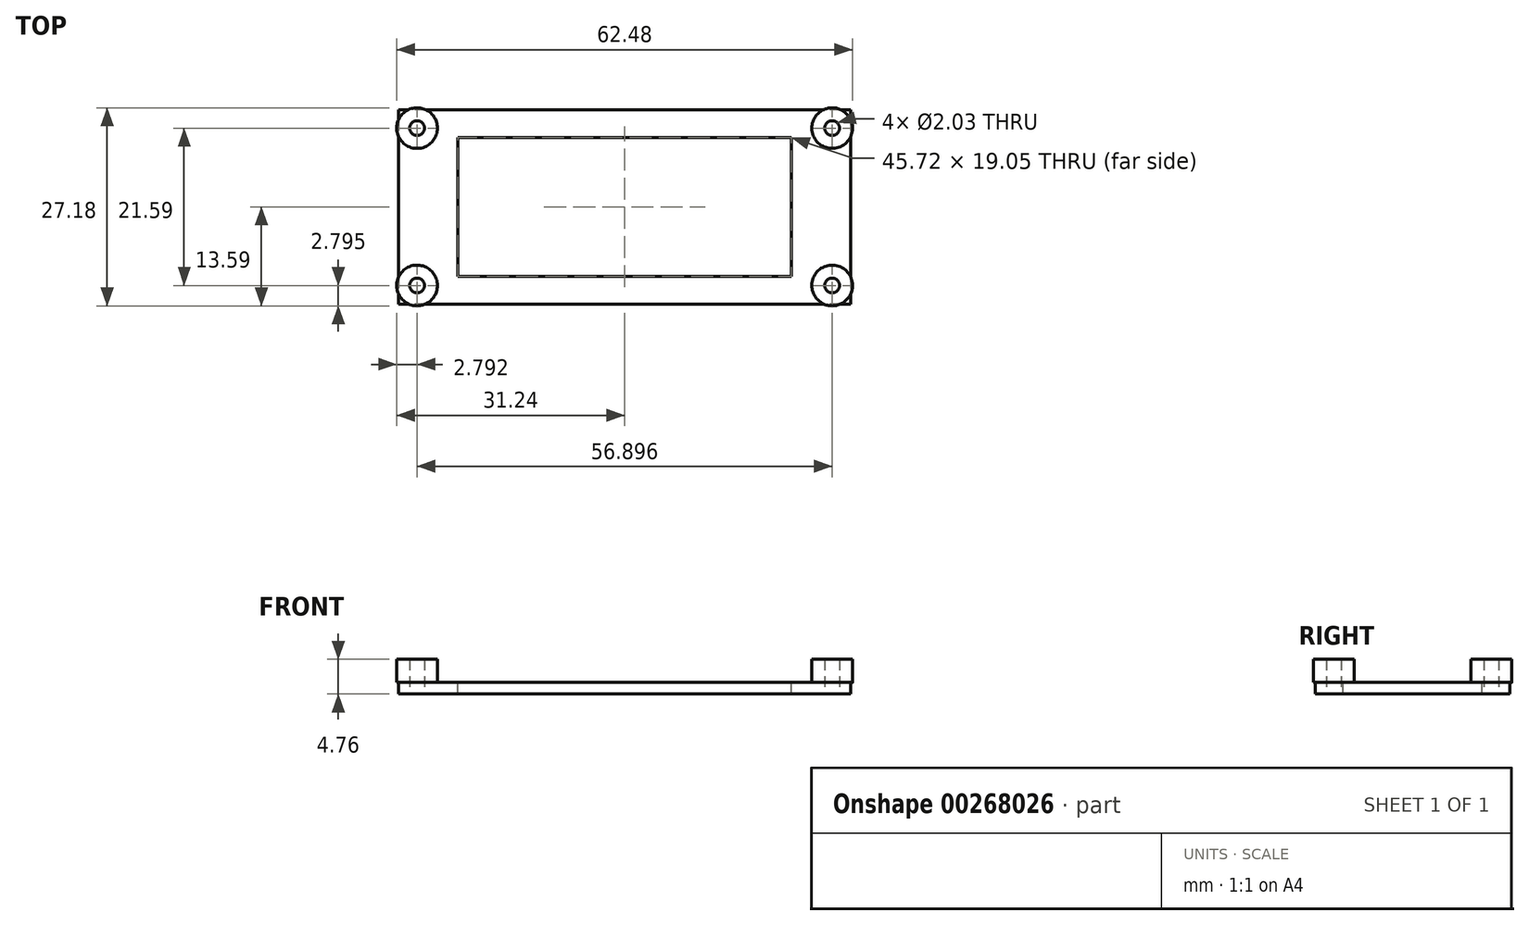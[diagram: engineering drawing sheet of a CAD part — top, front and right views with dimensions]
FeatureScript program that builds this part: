
annotation { "Feature Type Name" : "Feature", "Feature Type Description" : "" }
export const myFeature = defineFeature(function(context is Context, id is Id, definition is map)
    precondition{}
    {
        {
            var Q0;
            Q0=qCreatedBy(makeId("Top.planeOp"),FACE);
            var sketch = newSketch(context, id + "F0", { "sketchPlane" : qUnion([Q0])});
            skLineSegment(sketch, "E0.bottom", {"start": v(30.99, 13.33) * mm, "end": v(-30.99, 13.34) * mm});
            skLineSegment(sketch, "E0.top", {"start": v(30.99, -13.34) * mm, "end": v(-30.99, -13.34) * mm});
            skLineSegment(sketch, "E0.left", {"start": v(30.99, 13.33) * mm, "end": v(30.99, -13.34) * mm});
            skLineSegment(sketch, "E0.right", {"start": v(-30.99, 13.34) * mm, "end": v(-30.99, -13.34) * mm});
            skPoint(sketch, "E0.middle", {"position": v(0, 0) * mm});
            skSolve(sketch);
        }
        {
            var Q0;
            Q0=makeQuery(id+"F0.imprint","IMPRINT",FACE,{"disambiguationData":[TD([[makeQuery(id+"F0.imprint","IMPRINT",EDGE,{"derivedFrom":sQuery(id+"F0.wireOp",EDGE,"E0.bottom")}),1.0]])]});
            extrude(context, id + "F1", {"entities" : qUnion([Q0]), "depth" : 1.59 * mm});
        }
        {
            var Q0;
            Q0=makeQuery(id+"F1.opExtrude","CAP_FACE",FACE,{"disambiguationData":[OSD([sQuery(id+"F0.wireOp",EDGE,"E0.bottom"),sQuery(id+"F0.wireOp",EDGE,"E0.top"),sQuery(id+"F0.wireOp",EDGE,"E0.left"),sQuery(id+"F0.wireOp",EDGE,"E0.right")])],"isStart":false});
            var sketch = newSketch(context, id + "F2", { "sketchPlane" : qUnion([Q0])});
            skLineSegment(sketch, "E1.bottom", {"start": v(28.45, -13.34) * mm, "end": v(30.99, -13.34) * mm, "construction": true});
            skLineSegment(sketch, "E1.top", {"start": v(28.45, -10.8) * mm, "end": v(30.99, -10.8) * mm, "construction": true});
            skLineSegment(sketch, "E1.left", {"start": v(28.45, -13.34) * mm, "end": v(28.45, -10.8) * mm, "construction": true});
            skLineSegment(sketch, "E1.right", {"start": v(30.99, -13.34) * mm, "end": v(30.99, -10.8) * mm, "construction": true});
            skCircle(sketch, "E2", {"center": v(28.45, -10.8) * mm, "radius": 1.02 * mm});
            skCircle(sketch, "E3", {"center": v(28.45, -10.8) * mm, "radius": 2.8 * mm});
            skCircle(sketch, "E4", {"center": v(-28.45, 10.8) * mm, "radius": 1.02 * mm});
            skCircle(sketch, "E5", {"center": v(-28.45, 10.8) * mm, "radius": 2.8 * mm});
            skCircle(sketch, "E6", {"center": v(-28.45, -10.8) * mm, "radius": 1.02 * mm});
            skCircle(sketch, "E7", {"center": v(-28.45, -10.8) * mm, "radius": 2.8 * mm});
            skLineSegment(sketch, "E8.bottom", {"start": v(30.99, 13.33) * mm, "end": v(28.45, 13.33) * mm, "construction": true});
            skLineSegment(sketch, "E8.top", {"start": v(30.99, 10.8) * mm, "end": v(28.45, 10.8) * mm, "construction": true});
            skLineSegment(sketch, "E8.left", {"start": v(30.99, 13.33) * mm, "end": v(30.99, 10.8) * mm, "construction": true});
            skLineSegment(sketch, "E8.right", {"start": v(28.45, 13.33) * mm, "end": v(28.45, 10.8) * mm, "construction": true});
            skLineSegment(sketch, "E9.bottom", {"start": v(-30.99, 13.34) * mm, "end": v(-28.45, 13.34) * mm, "construction": true});
            skLineSegment(sketch, "E9.top", {"start": v(-30.99, 10.8) * mm, "end": v(-28.45, 10.8) * mm, "construction": true});
            skLineSegment(sketch, "E9.left", {"start": v(-30.99, 13.34) * mm, "end": v(-30.99, 10.8) * mm, "construction": true});
            skLineSegment(sketch, "E9.right", {"start": v(-28.45, 13.34) * mm, "end": v(-28.45, 10.8) * mm, "construction": true});
            skLineSegment(sketch, "E10.bottom", {"start": v(-30.99, -13.34) * mm, "end": v(-28.45, -13.34) * mm, "construction": true});
            skLineSegment(sketch, "E10.top", {"start": v(-30.99, -10.8) * mm, "end": v(-28.45, -10.8) * mm, "construction": true});
            skLineSegment(sketch, "E10.left", {"start": v(-30.99, -13.34) * mm, "end": v(-30.99, -10.8) * mm, "construction": true});
            skLineSegment(sketch, "E10.right", {"start": v(-28.45, -13.34) * mm, "end": v(-28.45, -10.8) * mm, "construction": true});
            skCircle(sketch, "E11", {"center": v(28.45, 10.8) * mm, "radius": 1.02 * mm});
            skCircle(sketch, "E12", {"center": v(28.45, 10.8) * mm, "radius": 2.8 * mm});
            skSolve(sketch);
        }
        {
            var Q0;
            Q0=makeQuery(id+"F2.imprint","IMPRINT",FACE,{"disambiguationData":[TD([[makeQuery(id+"F2.imprint","IMPRINT",EDGE,{"derivedFrom":sQuery(id+"F2.wireOp",EDGE,"E4")}),-1.0]])]});
            var Q1;
            Q1=qSketchRegion(id+"F2",true);
            var Q2;
            Q2=makeQuery(id+"F2.imprint","IMPRINT",FACE,{"disambiguationData":[TD([[makeQuery(id+"F2.imprint","IMPRINT",EDGE,{"derivedFrom":sQuery(id+"F2.wireOp",EDGE,"E2")}),-1.0]])]});
            extrude(context, id + "F3", {"entities" : qUnion([Q0, Q1, Q2]), "operationType" : NewBodyOperationType.ADD, "depth" : 3.17 * mm});
        }
        {
            var Q0;
            Q0=makeQuery(id+"F2.imprint","IMPRINT",FACE,{"disambiguationData":[TD([[makeQuery(id+"F2.imprint","IMPRINT",EDGE,{"derivedFrom":sQuery(id+"F2.wireOp",EDGE,"E4")}),1.0]])]});
            var Q1;
            Q1=makeQuery(id+"F2.imprint","IMPRINT",FACE,{"disambiguationData":[TD([[makeQuery(id+"F2.imprint","IMPRINT",EDGE,{"derivedFrom":sQuery(id+"F2.wireOp",EDGE,"E2")}),1.0]])]});
            var Q2;
            Q2=makeQuery(id+"F2.imprint","IMPRINT",FACE,{"disambiguationData":[TD([[makeQuery(id+"F2.imprint","IMPRINT",EDGE,{"derivedFrom":sQuery(id+"F2.wireOp",EDGE,"E11")}),1.0]])]});
            var Q3;
            Q3=makeQuery(id+"F2.imprint","IMPRINT",FACE,{"disambiguationData":[TD([[makeQuery(id+"F2.imprint","IMPRINT",EDGE,{"derivedFrom":sQuery(id+"F2.wireOp",EDGE,"E6")}),1.0]])]});
            extrude(context, id + "F4", {"entities" : qUnion([Q0, Q1, Q2, Q3]), "operationType" : NewBodyOperationType.REMOVE, "oppositeDirection" : true, "depth" : 12.7 * mm, "offsetDistance" : 25.4 * mm});
        }
        {
            var Q0;
            {var subQ0=sQuery(id+"F0.wireOp",EDGE,"E0.left");var subQ1=sQuery(id+"F0.wireOp",EDGE,"E0.top");var subQ2=sQuery(id+"F0.wireOp",EDGE,"E0.right");var subQ3=sQuery(id+"F0.wireOp",EDGE,"E0.bottom");Q0=makeQuery(id+"F3.boolean.opBoolean","SPLIT",FACE,{"disambiguationData":[TD([makeQuery(id+"F1.opExtrude","SWEPT_FACE",FACE,{"disambiguationData":[OSD([subQ3])]})])],"derivedFrom":makeQuery(id+"F1.opExtrude","CAP_FACE",FACE,{"disambiguationData":[OSD([subQ3,subQ1,subQ0,subQ2])],"isStart":false})});}
            var sketch = newSketch(context, id + "F5", { "sketchPlane" : qUnion([Q0])});
            skPoint(sketch, "E13.middle", {"position": v(0, 0) * mm});
            skLineSegment(sketch, "E14.bottom", {"start": v(22.86, -9.52) * mm, "end": v(-22.86, -9.53) * mm});
            skLineSegment(sketch, "E14.top", {"start": v(22.86, 9.53) * mm, "end": v(-22.86, 9.52) * mm});
            skLineSegment(sketch, "E14.left", {"start": v(22.86, -9.53) * mm, "end": v(22.86, 9.53) * mm});
            skLineSegment(sketch, "E14.right", {"start": v(-22.86, -9.53) * mm, "end": v(-22.86, 9.52) * mm});
            skSolve(sketch);
        }
        {
            var Q0;
            Q0=makeQuery(id+"F5.imprint","IMPRINT",FACE,{"disambiguationData":[TD([[makeQuery(id+"F5.imprint","IMPRINT",EDGE,{"derivedFrom":sQuery(id+"F5.wireOp",EDGE,"E14.bottom")}),-1.0]])]});
            extrude(context, id + "F6", {"entities" : qUnion([Q0]), "operationType" : NewBodyOperationType.REMOVE, "oppositeDirection" : true, "depth" : 6.35 * mm, "offsetDistance" : 25.4 * mm});
        }
    });
